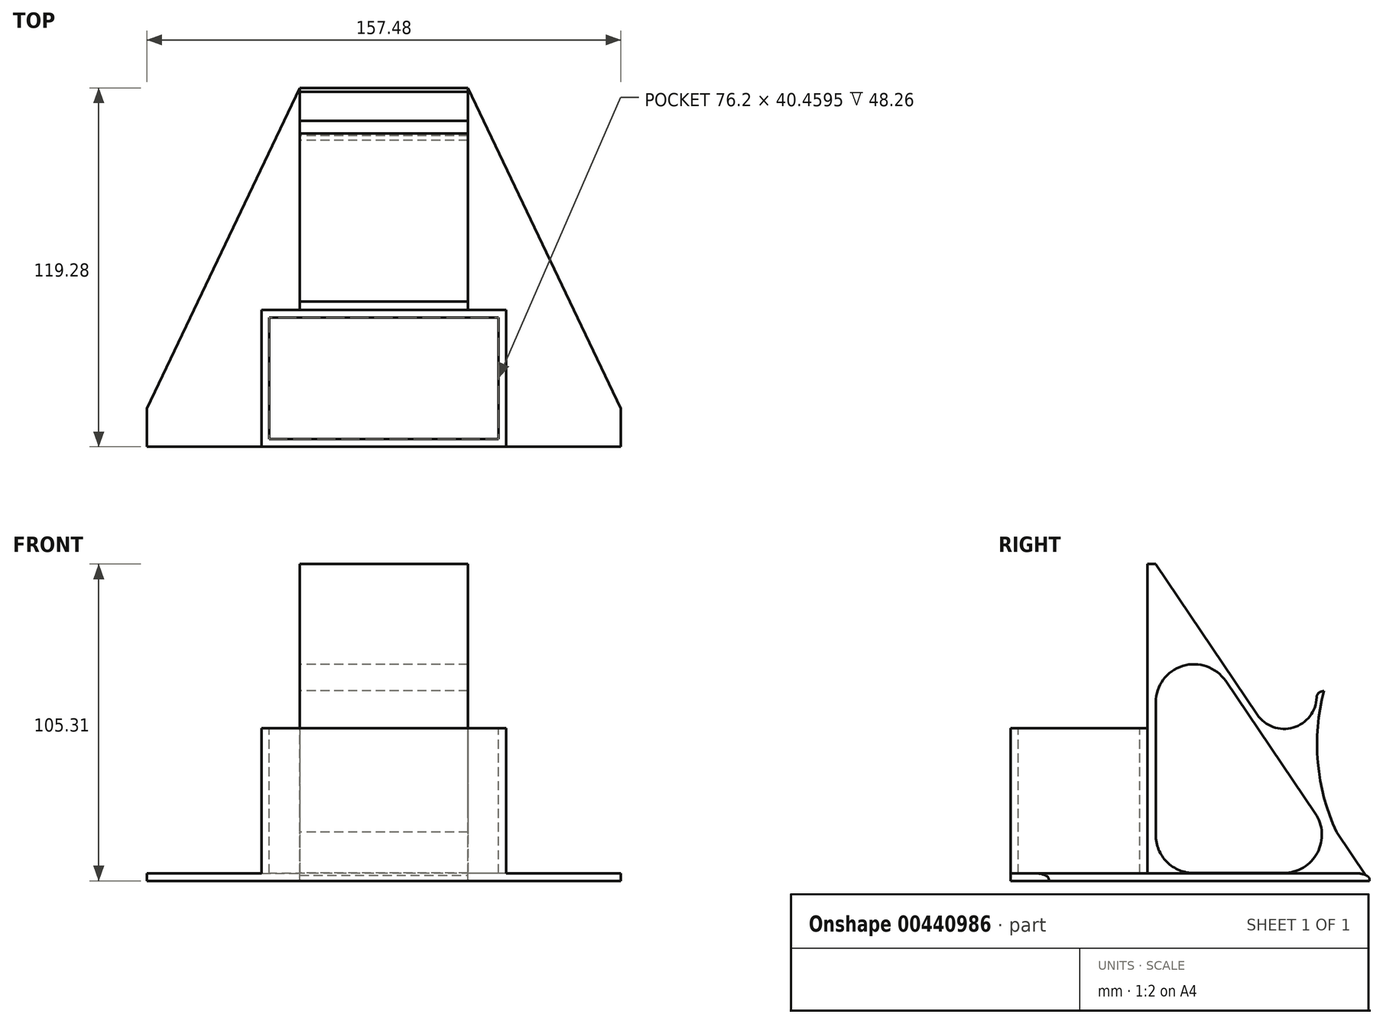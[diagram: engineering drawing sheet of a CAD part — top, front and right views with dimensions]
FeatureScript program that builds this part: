
annotation { "Feature Type Name" : "Feature", "Feature Type Description" : "" }
export const myFeature = defineFeature(function(context is Context, id is Id, definition is map)
    precondition{}
    {
        {
            var Q0;
            Q0=qCreatedBy(makeId("Right.planeOp"),FACE);
            var sketch = newSketch(context, id + "F0", { "sketchPlane" : qUnion([Q0])});
            skLineSegment(sketch, "E0", {"start": v(0, 0) * mm, "end": v(-10.96, 16.25) * mm});
            skLineSegment(sketch, "E1", {"start": v(-71.02, 0) * mm, "end": v(-101.5, 0) * mm});
            skLineSegment(sketch, "E2", {"start": v(-101.5, 0) * mm, "end": v(-101.5, 50.8) * mm});
            skLineSegment(sketch, "E3", {"start": v(-101.5, 50.8) * mm, "end": v(-73.74, 50.8) * mm});
            skLineSegment(sketch, "E4", {"start": v(0, 0) * mm, "end": v(-71.02, 0) * mm});
            skLineSegment(sketch, "E5", {"start": v(-71.02, 50.8) * mm, "end": v(-71.02, 15.26) * mm});
            skLineSegment(sketch, "E6", {"start": v(-17.62, 62.57) * mm, "end": v(-15.14, 63.14) * mm});
            skArc(sketch, "E7", {"start": v(-15.14, 63.14) * mm, "mid": v(-17.15, 39.33) * mm, "end": v(-10.96, 16.25) * mm});
            skArc(sketch, "E8", {"start": v(-37.29, 55.27) * mm, "mid": v(-24.59, 51.2) * mm, "end": v(-17.62, 62.57) * mm});
            skLineSegment(sketch, "E9.trimOffspring", {"start": v(-18.01, 22.42) * mm, "end": v(-47.8, 66.44) * mm});
            skLineSegment(sketch, "E10.trimOffspring", {"start": v(-28.51, 2.6) * mm, "end": v(-58.3, 2.56) * mm});
            skLineSegment(sketch, "E11.trimOffspring", {"start": v(-37.29, 55.27) * mm, "end": v(-71.02, 105.28) * mm});
            skLineSegment(sketch, "E12", {"start": v(-73.74, 104.75) * mm, "end": v(-73.74, 0) * mm});
            skLineSegment(sketch, "E13", {"start": v(-71.02, 50.8) * mm, "end": v(-71.02, 59.32) * mm});
            skLineSegment(sketch, "E14", {"start": v(-73.74, 104.75) * mm, "end": v(-73.74, 111.1) * mm});
            skLineSegment(sketch, "E15", {"start": v(-71.02, 105.28) * mm, "end": v(-71.02, 113.44) * mm});
            skLineSegment(sketch, "E16", {"start": v(-71.02, 113.44) * mm, "end": v(-73.74, 113.44) * mm});
            skLineSegment(sketch, "E17", {"start": v(-73.74, 113.44) * mm, "end": v(-73.74, 111.1) * mm});
            skPoint(sketch, "E18.visualSharp", {"position": v(-4.62, 2.64) * mm});
            skArc(sketch, "E18.filletArc", {"start": v(-28.51, 2.6) * mm, "mid": v(-17.3, 9.36) * mm, "end": v(-18.01, 22.42) * mm});
            skPoint(sketch, "E19.visualSharp", {"position": v(-71.02, 100.74) * mm});
            skArc(sketch, "E19.filletArc", {"start": v(-47.8, 66.44) * mm, "mid": v(-62.05, 71.46) * mm, "end": v(-71.02, 59.32) * mm});
            skPoint(sketch, "E20.visualSharp", {"position": v(-71.02, 2.54) * mm});
            skArc(sketch, "E20.filletArc", {"start": v(-71.02, 15.26) * mm, "mid": v(-67.3, 6.27) * mm, "end": v(-58.3, 2.56) * mm});
            skSolve(sketch);
        }
        {
            var Q0;
            Q0=makeQuery(id+"F0.imprint","IMPRINT",FACE,{"disambiguationData":[TD([[makeQuery(id+"F0.imprint","IMPRINT",EDGE,{"derivedFrom":sQuery(id+"F0.wireOp",EDGE,"E0")}),1.0]])]});
            extrude(context, id + "F1", {"entities" : qUnion([Q0]), "depth" : 50.8 * mm, "offsetDistance" : 25.4 * mm});
        }
        {
            var Q0;
            {var subQ0=sQuery(id+"F0.wireOp",EDGE,"E2");Q0=makeQuery(id+"F0.imprint","IMPRINT",FACE,{"disambiguationData":[TD([[makeQuery(id+"F0.imprint","IMPRINT",EDGE,{"derivedFrom":subQ0}),-1.0]])]});}
            extrude(context, id + "F2", {"entities" : qUnion([Q0]), "operationType" : NewBodyOperationType.ADD, "depth" : 50.8 * mm, "offsetDistance" : 25.4 * mm});
        }
        {
            var Q0;
            {var subQ0=sQuery(id+"F0.wireOp",EDGE,"E12");var subQ1=sQuery(id+"F0.wireOp",EDGE,"E1");Q0=makeQuery(id+"F2.boolean.opBoolean","MERGE",FACE,{"derivedFrom":[makeQuery(id+"F1.opExtrude","CAP_FACE",FACE,{"disambiguationData":[OSD([sQuery(id+"F0.wireOp",EDGE,"E0"),subQ1,sQuery(id+"F0.wireOp",EDGE,"E4"),sQuery(id+"F0.wireOp",EDGE,"E5"),sQuery(id+"F0.wireOp",EDGE,"E6"),sQuery(id+"F0.wireOp",EDGE,"E7"),sQuery(id+"F0.wireOp",EDGE,"E8"),sQuery(id+"F0.wireOp",EDGE,"E9.trimOffspring"),sQuery(id+"F0.wireOp",EDGE,"E10.trimOffspring"),sQuery(id+"F0.wireOp",EDGE,"E11.trimOffspring"),subQ0,sQuery(id+"F0.wireOp",EDGE,"E13"),sQuery(id+"F0.wireOp",EDGE,"E14"),sQuery(id+"F0.wireOp",EDGE,"E15"),sQuery(id+"F0.wireOp",EDGE,"E16"),sQuery(id+"F0.wireOp",EDGE,"E17"),sQuery(id+"F0.wireOp",EDGE,"E18.filletArc"),sQuery(id+"F0.wireOp",EDGE,"E19.filletArc"),sQuery(id+"F0.wireOp",EDGE,"E20.filletArc")])],"isStart":false}),makeQuery(id+"F2.opExtrude","CAP_FACE",FACE,{"disambiguationData":[OSD([subQ1,sQuery(id+"F0.wireOp",EDGE,"E2"),sQuery(id+"F0.wireOp",EDGE,"E3"),subQ0])],"isStart":false})]});}
            extrude(context, id + "F3", {"entities" : qUnion([Q0]), "operationType" : NewBodyOperationType.ADD, "depth" : 5.08 * mm, "offsetDistance" : 25.4 * mm});
        }
        {
            var Q0;
            {var subQ0=sQuery(id+"F0.wireOp",EDGE,"E3");Q0=makeQuery(id+"F3.boolean.opBoolean","MERGE",FACE,{"derivedFrom":[makeQuery(id+"F2.opExtrude","SWEPT_FACE",FACE,{"disambiguationData":[OSD([subQ0])]}),makeQuery(id+"F3.opExtrude","SWEPT_FACE",FACE,{"disambiguationData":[OSD([subQ0])]})]});}
            var sketch = newSketch(context, id + "F4", { "sketchPlane" : qUnion([Q0])});
            skLineSegment(sketch, "E21.0", {"start": v(53.34, -98.96) * mm, "end": v(2.54, -98.96) * mm});
            skLineSegment(sketch, "E22.0", {"start": v(53.34, -98.96) * mm, "end": v(53.34, -76.28) * mm});
            skLineSegment(sketch, "E23.0", {"start": v(53.34, -76.28) * mm, "end": v(2.54, -76.28) * mm});
            skLineSegment(sketch, "E24.0", {"start": v(2.54, -98.96) * mm, "end": v(2.54, -76.28) * mm});
            skSolve(sketch);
        }
        {
            var Q0;
            Q0=makeQuery(id+"F4.imprint","IMPRINT",FACE,{"disambiguationData":[TD([[makeQuery(id+"F4.imprint","IMPRINT",EDGE,{"derivedFrom":sQuery(id+"F4.wireOp",EDGE,"E21.0")}),-1.0]])]});
            extrude(context, id + "F5", {"entities" : qUnion([Q0]), "operationType" : NewBodyOperationType.REMOVE, "oppositeDirection" : true, "depth" : 48.26 * mm, "offsetDistance" : 25.4 * mm});
        }
        {
            var Q0;
            {var subQ0=sQuery(id+"F0.wireOp",EDGE,"E2");Q0=makeQuery(id+"F3.boolean.opBoolean","MERGE",FACE,{"derivedFrom":[makeQuery(id+"F2.opExtrude","SWEPT_FACE",FACE,{"disambiguationData":[OSD([subQ0])]}),makeQuery(id+"F3.opExtrude","SWEPT_FACE",FACE,{"disambiguationData":[OSD([subQ0])]})]});}
            extrude(context, id + "F6", {"entities" : qUnion([Q0]), "operationType" : NewBodyOperationType.ADD, "depth" : 5.08 * mm, "offsetDistance" : 25.4 * mm});
        }
        {
            var Q0;
            Q0=makeQuery(id+"F5.boolean.opBoolean","COPY",FACE,{"derivedFrom":makeQuery(id+"F5.opExtrude","SWEPT_FACE",FACE,{"disambiguationData":[OSD([sQuery(id+"F4.wireOp",EDGE,"E21.0")])]})});
            extrude(context, id + "F7", {"entities" : qUnion([Q0]), "operationType" : NewBodyOperationType.REMOVE, "oppositeDirection" : true, "depth" : 5.08 * mm, "offsetDistance" : 25.4 * mm});
        }
        {
            var Q0;
            {var subQ0=sQuery(id+"F0.wireOp",EDGE,"E1");var subQ1=sQuery(id+"F0.wireOp",EDGE,"E4");Q0=makeQuery(id+"F6.boolean.opBoolean","MERGE",FACE,{"derivedFrom":[makeQuery(id+"F3.boolean.opBoolean","MERGE",FACE,{"derivedFrom":[makeQuery(id+"F2.boolean.opBoolean","MERGE",FACE,{"derivedFrom":[makeQuery(id+"F1.opExtrude","SWEPT_FACE",FACE,{"disambiguationData":[OSD([subQ0,subQ1])]}),makeQuery(id+"F2.opExtrude","SWEPT_FACE",FACE,{"disambiguationData":[OSD([subQ0])]})]}),makeQuery(id+"F3.opExtrude","SWEPT_FACE",FACE,{"disambiguationData":[OSD([subQ0,subQ1])]})]}),makeQuery(id+"F6.opExtrude","SWEPT_FACE",FACE,{"disambiguationData":[OSD([subQ0,sQuery(id+"F0.wireOp",EDGE,"E2")])]})]});}
            var sketch = newSketch(context, id + "F8", { "sketchPlane" : qUnion([Q0])});
            skLineSegment(sketch, "E25", {"start": v(0, 106.58) * mm, "end": v(-50.8, 106.58) * mm});
            skLineSegment(sketch, "E26", {"start": v(55.88, 106.58) * mm, "end": v(106.68, 106.58) * mm});
            skLineSegment(sketch, "E27", {"start": v(106.68, 106.58) * mm, "end": v(55.88, 0) * mm});
            skLineSegment(sketch, "E28", {"start": v(-50.8, 106.58) * mm, "end": v(0, 0) * mm});
            skSolve(sketch);
        }
        {
            var Q0;
            Q0=makeQuery(id+"F8.imprint","IMPRINT",FACE,{"disambiguationData":[TD([[makeQuery(id+"F8.imprint","IMPRINT",EDGE,{"derivedFrom":sQuery(id+"F8.wireOp",EDGE,"E25")}),1.0]])]});
            extrude(context, id + "F9", {"entities" : qUnion([Q0]), "operationType" : NewBodyOperationType.ADD, "oppositeDirection" : true, "depth" : 2.54 * mm, "offsetDistance" : 25.4 * mm});
        }
        {
            var Q0;
            Q0=makeQuery(id+"F8.imprint","IMPRINT",FACE,{"disambiguationData":[TD([[makeQuery(id+"F8.imprint","IMPRINT",EDGE,{"derivedFrom":sQuery(id+"F8.wireOp",EDGE,"E26")}),-1.0]])]});
            extrude(context, id + "F10", {"entities" : qUnion([Q0]), "operationType" : NewBodyOperationType.ADD, "oppositeDirection" : true, "depth" : 2.54 * mm, "offsetDistance" : 25.4 * mm});
        }
        {
            var Q0;
            {var subQ0=sQuery(id+"F0.wireOp",EDGE,"E2");Q0=makeQuery(id+"F6.boolean.opBoolean","MERGE",FACE,{"derivedFrom":[makeQuery(id+"F3.opExtrude","CAP_FACE",FACE,{"disambiguationData":[OSD([sQuery(id+"F0.wireOp",EDGE,"E0"),sQuery(id+"F0.wireOp",EDGE,"E1"),subQ0,sQuery(id+"F0.wireOp",EDGE,"E3"),sQuery(id+"F0.wireOp",EDGE,"E4"),sQuery(id+"F0.wireOp",EDGE,"E5"),sQuery(id+"F0.wireOp",EDGE,"E6"),sQuery(id+"F0.wireOp",EDGE,"E7"),sQuery(id+"F0.wireOp",EDGE,"E8"),sQuery(id+"F0.wireOp",EDGE,"E9.trimOffspring"),sQuery(id+"F0.wireOp",EDGE,"E10.trimOffspring"),sQuery(id+"F0.wireOp",EDGE,"E11.trimOffspring"),sQuery(id+"F0.wireOp",EDGE,"E12"),sQuery(id+"F0.wireOp",EDGE,"E13"),sQuery(id+"F0.wireOp",EDGE,"E14"),sQuery(id+"F0.wireOp",EDGE,"E15"),sQuery(id+"F0.wireOp",EDGE,"E16"),sQuery(id+"F0.wireOp",EDGE,"E17"),sQuery(id+"F0.wireOp",EDGE,"E18.filletArc"),sQuery(id+"F0.wireOp",EDGE,"E19.filletArc"),sQuery(id+"F0.wireOp",EDGE,"E20.filletArc")])],"isStart":false}),makeQuery(id+"F6.opExtrude","SWEPT_FACE",FACE,{"disambiguationData":[OSD([subQ0]),TDD([makeQuery(id+"F3.opExtrude","CAP_EDGE",EDGE,{"disambiguationData":[OSD([subQ0])],"isStart":false})])]})]});}
            var sketch = newSketch(context, id + "F11", { "sketchPlane" : qUnion([Q0])});
            skLineSegment(sketch, "E29", {"start": v(-73.74, 50.8) * mm, "end": v(-72.65, 47) * mm});
            skLineSegment(sketch, "E30", {"start": v(-73.74, 2.54) * mm, "end": v(-73.74, 50.8) * mm});
            skSolve(sketch);
        }
        {
            var Q0;
            Q0 = qSketchRegion(id + "F11", true);
            var Q1;
            {var subQ0=sQuery(id+"F11.wireOp",EDGE,"E30");Q1=makeQuery(id+"F11.imprint","IMPRINT",FACE,{"disambiguationData":[TD([[makeQuery(id+"F11.imprint","IMPRINT",EDGE,{"derivedFrom":subQ0}),1.0]])]});}
            extrude(context, id + "F12", {"entities" : qUnion([Q0, Q1]), "operationType" : NewBodyOperationType.ADD, "depth" : 12.7 * mm, "offsetDistance" : 25.4 * mm});
        }
        {
            var Q0;
            {var subQ0=sQuery(id+"F4.wireOp",EDGE,"E22.0");Q0=makeQuery(id+"F7.boolean.opBoolean","MERGE",FACE,{"derivedFrom":[makeQuery(id+"F5.boolean.opBoolean","COPY",FACE,{"derivedFrom":makeQuery(id+"F5.opExtrude","SWEPT_FACE",FACE,{"disambiguationData":[OSD([subQ0])]})}),makeQuery(id+"F7.opExtrude","SWEPT_FACE",FACE,{"disambiguationData":[OSD([sQuery(id+"F4.wireOp",EDGE,"E21.0"),subQ0])]})]});}
            extrude(context, id + "F13", {"entities" : qUnion([Q0]), "operationType" : NewBodyOperationType.REMOVE, "oppositeDirection" : true, "depth" : 12.7 * mm, "offsetDistance" : 25.4 * mm});
        }
        {
            var Q0;
            {var subQ0=sQuery(id+"F0.wireOp",EDGE,"E2");Q0=makeQuery(id+"F0.imprint","IMPRINT",FACE,{"disambiguationData":[TD([[makeQuery(id+"F0.imprint","IMPRINT",EDGE,{"derivedFrom":subQ0}),-1.0]])]});}
            extrude(context, id + "F14", {"entities" : qUnion([Q0]), "operationType" : NewBodyOperationType.ADD, "oppositeDirection" : true, "depth" : 12.7 * mm, "offsetDistance" : 25.4 * mm});
        }
        {
            var Q0;
            {var subQ0=sQuery(id+"F0.wireOp",EDGE,"E2");var subQ1=sQuery(id+"F0.wireOp",EDGE,"E3");var subQ3=sQuery(id+"F0.wireOp",EDGE,"E4");var subQ4=sQuery(id+"F0.wireOp",EDGE,"E1");var subQ5=sQuery(id+"F0.wireOp",EDGE,"E12");Q0=makeQuery(id+"F14.boolean.opBoolean","SPLIT",FACE,{"disambiguationData":[TD([makeQuery(id+"F6.opExtrude","CAP_FACE",FACE,{"disambiguationData":[OSD([subQ0])],"isStart":false})])],"derivedFrom":makeQuery(id+"F6.boolean.opBoolean","MERGE",FACE,{"derivedFrom":[makeQuery(id+"F2.boolean.opBoolean","MERGE",FACE,{"derivedFrom":[makeQuery(id+"F1.opExtrude","CAP_FACE",FACE,{"disambiguationData":[OSD([sQuery(id+"F0.wireOp",EDGE,"E0"),subQ4,subQ3,sQuery(id+"F0.wireOp",EDGE,"E5"),sQuery(id+"F0.wireOp",EDGE,"E6"),sQuery(id+"F0.wireOp",EDGE,"E7"),sQuery(id+"F0.wireOp",EDGE,"E8"),sQuery(id+"F0.wireOp",EDGE,"E9.trimOffspring"),sQuery(id+"F0.wireOp",EDGE,"E10.trimOffspring"),sQuery(id+"F0.wireOp",EDGE,"E11.trimOffspring"),subQ5,sQuery(id+"F0.wireOp",EDGE,"E13"),sQuery(id+"F0.wireOp",EDGE,"E14"),sQuery(id+"F0.wireOp",EDGE,"E15"),sQuery(id+"F0.wireOp",EDGE,"E16"),sQuery(id+"F0.wireOp",EDGE,"E17"),sQuery(id+"F0.wireOp",EDGE,"E18.filletArc"),sQuery(id+"F0.wireOp",EDGE,"E19.filletArc"),sQuery(id+"F0.wireOp",EDGE,"E20.filletArc")])],"isStart":true}),makeQuery(id+"F2.opExtrude","CAP_FACE",FACE,{"disambiguationData":[OSD([subQ4,subQ0,subQ1,subQ5])],"isStart":true})]}),makeQuery(id+"F6.opExtrude","SWEPT_FACE",FACE,{"disambiguationData":[OSD([subQ0]),TDD([makeQuery(id+"F2.opExtrude","CAP_EDGE",EDGE,{"disambiguationData":[OSD([subQ0])],"isStart":true})])]})]})});}
            var sketch = newSketch(context, id + "F15", { "sketchPlane" : qUnion([Q0])});
            skLineSegment(sketch, "E31", {"start": v(101.5, 50.8) * mm, "end": v(101.5, 2.54) * mm});
            skLineSegment(sketch, "E32", {"start": v(101.5, 2.54) * mm, "end": v(106.58, 2.54) * mm});
            skLineSegment(sketch, "E33", {"start": v(106.58, 2.54) * mm, "end": v(106.58, 50.8) * mm});
            skLineSegment(sketch, "E34", {"start": v(106.58, 50.8) * mm, "end": v(101.5, 50.8) * mm});
            skSolve(sketch);
        }
        {
            var Q0;
            Q0 = qSketchRegion(id + "F15", true);
            extrude(context, id + "F16", {"entities" : qUnion([Q0]), "operationType" : NewBodyOperationType.ADD, "depth" : 12.7 * mm, "offsetDistance" : 25.4 * mm});
        }
        {
            var Q0;
            {var subQ0=sQuery(id+"F4.wireOp",EDGE,"E24.0");Q0=makeQuery(id+"F7.boolean.opBoolean","MERGE",FACE,{"derivedFrom":[makeQuery(id+"F5.boolean.opBoolean","COPY",FACE,{"derivedFrom":makeQuery(id+"F5.opExtrude","SWEPT_FACE",FACE,{"disambiguationData":[OSD([subQ0])]})}),makeQuery(id+"F7.opExtrude","SWEPT_FACE",FACE,{"disambiguationData":[OSD([sQuery(id+"F4.wireOp",EDGE,"E21.0"),subQ0])]})]});}
            extrude(context, id + "F17", {"entities" : qUnion([Q0]), "operationType" : NewBodyOperationType.REMOVE, "oppositeDirection" : true, "depth" : 12.7 * mm, "offsetDistance" : 25.4 * mm});
        }
        {
            var Q0;
            {var subQ0=sQuery(id+"F0.wireOp",EDGE,"E2");Q0=makeQuery(id+"F16.boolean.opBoolean","MERGE",FACE,{"derivedFrom":[makeQuery(id+"F12.boolean.opBoolean","MERGE",FACE,{"derivedFrom":[makeQuery(id+"F10.boolean.opBoolean","MERGE",FACE,{"derivedFrom":[makeQuery(id+"F9.boolean.opBoolean","MERGE",FACE,{"derivedFrom":[makeQuery(id+"F6.opExtrude","CAP_FACE",FACE,{"disambiguationData":[OSD([subQ0])],"isStart":false}),makeQuery(id+"F9.opExtrude","SWEPT_FACE",FACE,{"disambiguationData":[OSD([sQuery(id+"F8.wireOp",EDGE,"E25")])]})]}),makeQuery(id+"F10.opExtrude","SWEPT_FACE",FACE,{"disambiguationData":[OSD([sQuery(id+"F8.wireOp",EDGE,"E26")])]})]}),makeQuery(id+"F12.opExtrude","SWEPT_FACE",FACE,{"disambiguationData":[OSD([subQ0])]})]}),makeQuery(id+"F16.opExtrude","SWEPT_FACE",FACE,{"disambiguationData":[OSD([sQuery(id+"F15.wireOp",EDGE,"E33")])]})]});}
            extrude(context, id + "F18", {"entities" : qUnion([Q0]), "operationType" : NewBodyOperationType.ADD, "depth" : 12.7 * mm, "offsetDistance" : 25.4 * mm});
        }
        {
            var Q0;
            {var subQ0=sQuery(id+"F4.wireOp",EDGE,"E24.0");var subQ1=sQuery(id+"F4.wireOp",EDGE,"E21.0");var subQ2=sQuery(id+"F4.wireOp",EDGE,"E22.0");Q0=makeQuery(id+"F17.boolean.opBoolean","MERGE",FACE,{"derivedFrom":[makeQuery(id+"F13.boolean.opBoolean","MERGE",FACE,{"derivedFrom":[makeQuery(id+"F7.boolean.opBoolean","COPY",FACE,{"derivedFrom":makeQuery(id+"F7.opExtrude","CAP_FACE",FACE,{"disambiguationData":[OSD([subQ1])],"isStart":false})}),makeQuery(id+"F13.opExtrude","SWEPT_FACE",FACE,{"disambiguationData":[OSD([subQ1,subQ2]),TDD([makeQuery(id+"F7.boolean.opBoolean","COPY",EDGE,{"derivedFrom":makeQuery(id+"F7.opExtrude","CAP_EDGE",EDGE,{"disambiguationData":[OSD([subQ1,subQ2])],"isStart":false})})])]})]}),makeQuery(id+"F17.opExtrude","SWEPT_FACE",FACE,{"disambiguationData":[OSD([subQ1,subQ0]),TDD([makeQuery(id+"F7.boolean.opBoolean","COPY",EDGE,{"derivedFrom":makeQuery(id+"F7.opExtrude","CAP_EDGE",EDGE,{"disambiguationData":[OSD([subQ1,subQ0])],"isStart":false})})])]})]});}
            extrude(context, id + "F19", {"entities" : qUnion([Q0]), "operationType" : NewBodyOperationType.REMOVE, "oppositeDirection" : true, "depth" : 12.7 * mm, "offsetDistance" : 25.4 * mm});
        }
        {
            var Q0;
            {var subQ0=sQuery(id+"F0.wireOp",EDGE,"E16");Q0=makeQuery(id+"F3.boolean.opBoolean","MERGE",FACE,{"derivedFrom":[makeQuery(id+"F1.opExtrude","SWEPT_FACE",FACE,{"disambiguationData":[OSD([subQ0])]}),makeQuery(id+"F3.opExtrude","SWEPT_FACE",FACE,{"disambiguationData":[OSD([subQ0])]})]});}
            extrude(context, id + "F20", {"entities" : qUnion([Q0]), "operationType" : NewBodyOperationType.REMOVE, "oppositeDirection" : true, "depth" : 8.13 * mm, "offsetDistance" : 25.4 * mm});
        }
        {
            var Q0;
            Q0=makeQuery(id+"F10.opExtrude","CAP_EDGE",EDGE,{"disambiguationData":[OSD([sQuery(id+"F8.wireOp",EDGE,"E27")])],"isStart":false});
            var Q1;
            Q1=makeQuery(id+"F9.opExtrude","CAP_EDGE",EDGE,{"disambiguationData":[OSD([sQuery(id+"F8.wireOp",EDGE,"E28")])],"isStart":false});
            fillet(context, id + "F21", {"entities" : qUnion([Q0, Q1]), "radius" : 2.03 * mm, "tangentPropagation" : true, "allowEdgeOverflow" : false});
        }
        {
            var Q0;
            Q0=makeQuery(id+"F10.opExtrude","SWEPT_FACE",FACE,{"disambiguationData":[OSD([sQuery(id+"F0.wireOp",EDGE,"E1"),sQuery(id+"F0.wireOp",EDGE,"E2"),sQuery(id+"F0.wireOp",EDGE,"E4")])]});
            extrude(context, id + "F22", {"entities" : qUnion([Q0]), "operationType" : NewBodyOperationType.ADD, "depth" : 55.88 * mm, "offsetDistance" : 25.4 * mm});
        }
        {
            var Q0;
            {var subQ0=sQuery(id+"F0.wireOp",EDGE,"E8");var subQ1=sQuery(id+"F0.wireOp",EDGE,"E6");Q0=makeQuery(id+"F3.boolean.opBoolean","MERGE",EDGE,{"derivedFrom":[makeQuery(id+"F1.opExtrude","SWEPT_EDGE",EDGE,{"disambiguationData":[OSD([subQ1,subQ0])]}),makeQuery(id+"F3.opExtrude","SWEPT_EDGE",EDGE,{"disambiguationData":[OSD([subQ1,subQ0])]})]});}
            var Q1;
            Q1=makeQuery(id+"F20.boolean.opBoolean","COPY",EDGE,{"derivedFrom":makeQuery(id+"F20.opExtrude","CAP_EDGE",EDGE,{"disambiguationData":[OSD([sQuery(id+"F0.wireOp",EDGE,"E15"),sQuery(id+"F0.wireOp",EDGE,"E16")])],"isStart":false})});
            fillet(context, id + "F23", {"entities" : qUnion([Q0, Q1]), "radius" : 2.03 * mm, "tangentPropagation" : true, "allowEdgeOverflow" : false});
        }
        {
            var Q0;
            {var subQ0=sQuery(id+"F0.wireOp",EDGE,"E17");var subQ1=sQuery(id+"F0.wireOp",EDGE,"E14");var subQ2=sQuery(id+"F0.wireOp",EDGE,"E12");Q0=makeQuery(id+"F3.boolean.opBoolean","MERGE",FACE,{"derivedFrom":[makeQuery(id+"F1.opExtrude","SWEPT_FACE",FACE,{"disambiguationData":[OSD([subQ2,subQ1,subQ0])]}),makeQuery(id+"F3.opExtrude","SWEPT_FACE",FACE,{"disambiguationData":[OSD([subQ2,subQ1,subQ0])]})]});}
            var sketch = newSketch(context, id + "F24", { "sketchPlane" : qUnion([Q0])});
            skLineSegment(sketch, "E35.0", {"start": v(2.54, 104.75) * mm, "end": v(2.54, 0) * mm});
            skLineSegment(sketch, "E36.0", {"start": v(53.34, 105.31) * mm, "end": v(53.34, 50.8) * mm});
            skLineSegment(sketch, "E37", {"start": v(2.54, 104.75) * mm, "end": v(2.54, 105.31) * mm});
            skLineSegment(sketch, "E38.bottom", {"start": v(2.54, 105.31) * mm, "end": v(53.34, 105.31) * mm});
            skLineSegment(sketch, "E38.top", {"start": v(2.54, 50.8) * mm, "end": v(53.34, 50.8) * mm});
            skLineSegment(sketch, "E38.left", {"start": v(2.54, 105.31) * mm, "end": v(2.54, 50.8) * mm});
            skSolve(sketch);
        }
    });
